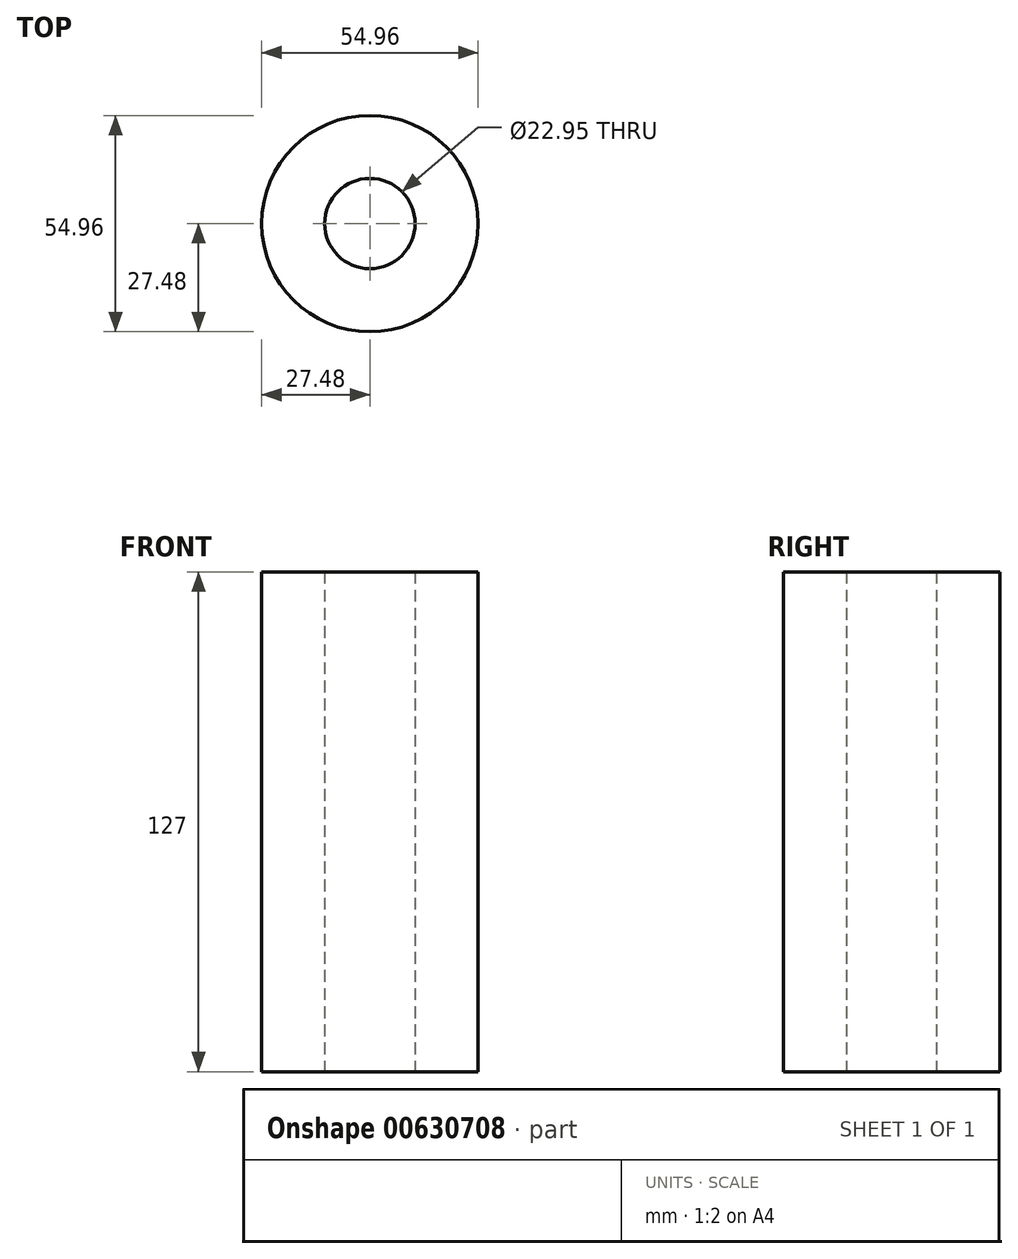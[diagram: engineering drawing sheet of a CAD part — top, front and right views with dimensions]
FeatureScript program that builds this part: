
annotation { "Feature Type Name" : "Feature", "Feature Type Description" : "" }
export const myFeature = defineFeature(function(context is Context, id is Id, definition is map)
    precondition{}
    {
        {
            var Q0;
            Q0=qCreatedBy(makeId("Top.planeOp"),FACE);
            var sketch = newSketch(context, id + "F0", { "sketchPlane" : qUnion([Q0])});
            skCircle(sketch, "E0", {"center": v(0, 0) * mm, "radius": 11.48 * mm});
            skCircle(sketch, "E1", {"center": v(0, 0) * mm, "radius": 27.48 * mm});
            skSolve(sketch);
        }
        {
            var Q0;
            Q0=makeQuery(id+"F0.imprint","IMPRINT",FACE,{"disambiguationData":[TD([[makeQuery(id+"F0.imprint","IMPRINT",EDGE,{"derivedFrom":sQuery(id+"F0.wireOp",EDGE,"E0")}),-1.0]])]});
            extrude(context, id + "F1", {"entities" : qUnion([Q0]), "depth" : 127 * mm, "offsetDistance" : 25.4 * mm});
        }
        {
            var Q0;
            Q0=qCreatedBy(makeId("Front.planeOp"),FACE);
            var sketch = newSketch(context, id + "F2", { "sketchPlane" : qUnion([Q0])});
            skCircle(sketch, "E2", {"center": v(-124.15, 27.5) * mm, "radius": 26.76 * mm});
            skSolve(sketch);
        }
        {
            var Q0;
            Q0=makeQuery(id+"F2.imprint","IMPRINT",FACE,{"disambiguationData":[TD([[makeQuery(id+"F2.imprint","IMPRINT",EDGE,{"derivedFrom":sQuery(id+"F2.wireOp",EDGE,"E2")}),1.0]])]});
            extrude(context, id + "F3", {"entities" : qUnion([Q0]), "endBound" : BoundingType.SYMMETRIC, "depth" : 76.2 * mm, "offsetDistance" : 25.4 * mm});
        }
        {
            var Q0;
            Q0=makeQuery(id+"F3.opExtrude","SWEPT_BODY",BODY,{"disambiguationData":[OSD([sQuery(id+"F2.wireOp",EDGE,"E2")])]});
            deleteBodies(context, id + "F4", {"entities" : qUnion([Q0])});
        }
    });
